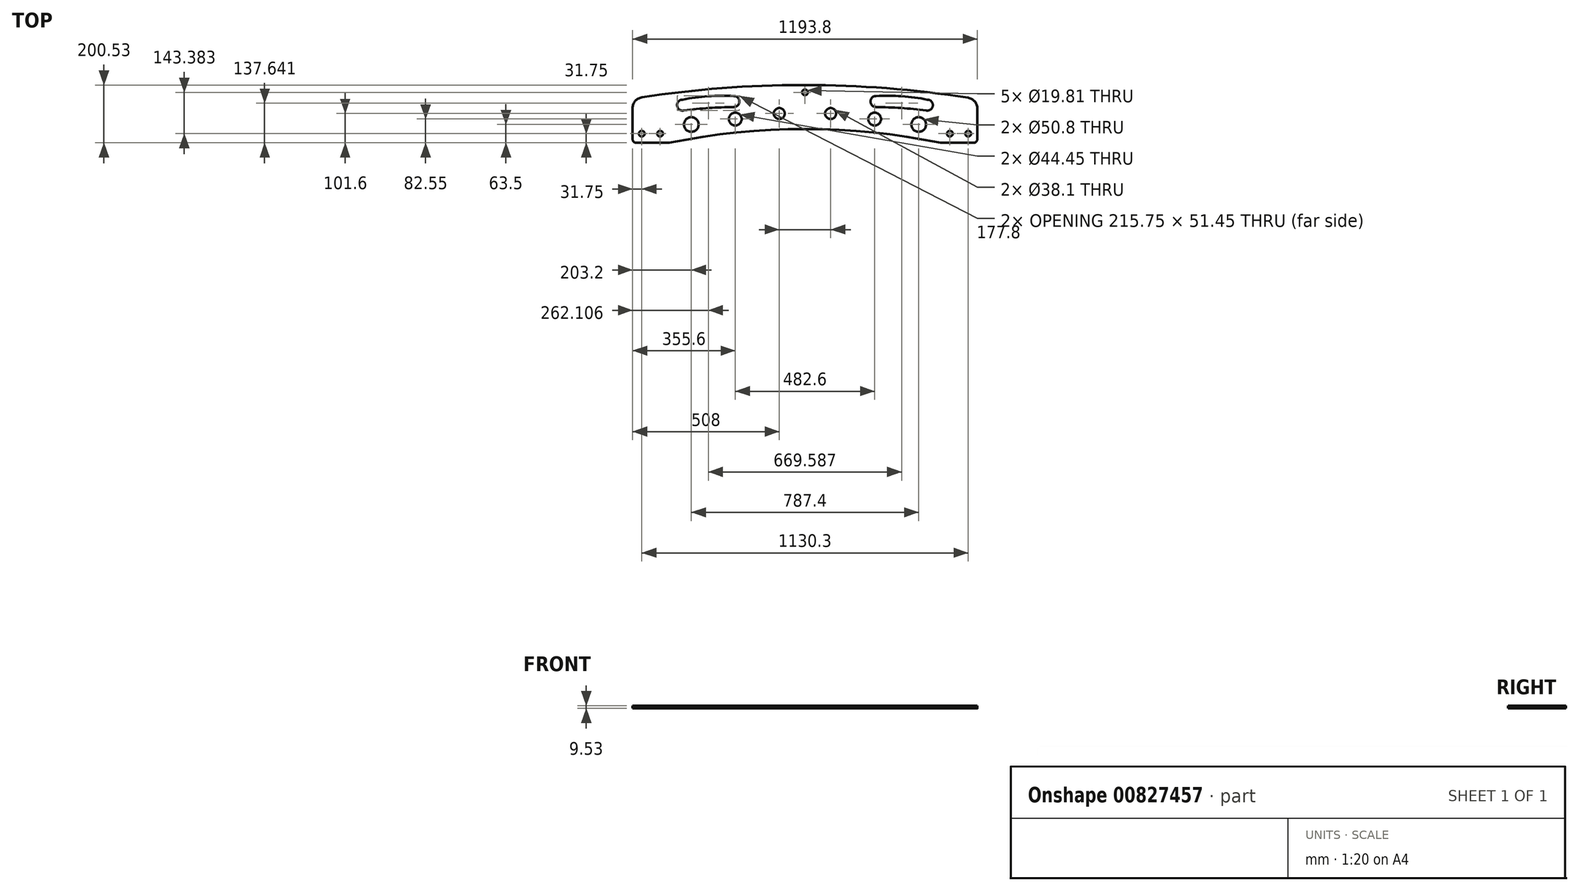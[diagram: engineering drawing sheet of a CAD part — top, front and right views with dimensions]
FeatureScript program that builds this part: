
annotation { "Feature Type Name" : "Feature", "Feature Type Description" : "" }
export const myFeature = defineFeature(function(context is Context, id is Id, definition is map)
    precondition{}
    {
        {
            var Q0;
            Q0=qCreatedBy(makeId("Top.planeOp"),FACE);
            var sketch = newSketch(context, id + "F0", { "sketchPlane" : qUnion([Q0])});
            skLineSegment(sketch, "E0.bottom", {"start": v(12.7, 0) * mm, "end": v(1181.1, 0) * mm});
            skLineSegment(sketch, "E0.top", {"start": v(-12.7, 200.53) * mm, "end": v(1206.5, 200.53) * mm});
            skLineSegment(sketch, "E0.left", {"start": v(0, 12.7) * mm, "end": v(0, 120.02) * mm});
            skLineSegment(sketch, "E0.right", {"start": v(1193.8, 12.7) * mm, "end": v(1193.8, 118.67) * mm});
            skPoint(sketch, "E1", {"position": v(127, 0) * mm});
            skPoint(sketch, "E2", {"position": v(1066.8, 0) * mm});
            skPoint(sketch, "E3", {"position": v(596.9, 0) * mm});
            skPoint(sketch, "E4", {"position": v(596.9, 48.13) * mm});
            skArc(sketch, "E5", {"start": v(1066.8, 0) * mm, "mid": v(596.9, 48.13) * mm, "end": v(127, 0) * mm});
            skPoint(sketch, "E6", {"position": v(0, 152.4) * mm});
            skPoint(sketch, "E7", {"position": v(1193.8, 152.4) * mm});
            skPoint(sketch, "E8", {"position": v(596.9, 200.53) * mm});
            skArc(sketch, "E9", {"start": v(1161.59, 156.31) * mm, "mid": v(597, 200.53) * mm, "end": v(32.3, 157.67) * mm});
            skPoint(sketch, "E10.visualSharp", {"position": v(0, 0) * mm});
            skArc(sketch, "E10.filletArc", {"start": v(0, 12.7) * mm, "mid": v(3.72, 3.72) * mm, "end": v(12.7, 0) * mm});
            skPoint(sketch, "E11.visualSharp", {"position": v(1193.8, 0) * mm});
            skArc(sketch, "E11.filletArc", {"start": v(1181.1, 0) * mm, "mid": v(1190.08, 3.72) * mm, "end": v(1193.8, 12.7) * mm});
            skCircle(sketch, "E12", {"center": v(596.9, 175.13) * mm, "radius": 9.9 * mm});
            skCircle(sketch, "E13", {"center": v(31.75, 31.75) * mm, "radius": 9.9 * mm});
            skCircle(sketch, "E14", {"center": v(1162.05, 31.75) * mm, "radius": 9.9 * mm});
            skArc(sketch, "E15", {"start": v(173.13, 149.73) * mm, "mid": v(154.23, 128.3) * mm, "end": v(177.88, 112.23) * mm});
            skArc(sketch, "E16", {"start": v(350.93, 124.33) * mm, "mid": v(369.98, 143.38) * mm, "end": v(350.93, 162.43) * mm});
            skArc(sketch, "E17", {"start": v(350.93, 124.33) * mm, "mid": v(261.85, 120.48) * mm, "end": v(173.13, 111.63) * mm});
            skArc(sketch, "E18", {"start": v(350.93, 162.43) * mm, "mid": v(261.64, 161.55) * mm, "end": v(173.13, 149.73) * mm});
            skLineSegment(sketch, "E19", {"start": v(596.9, 48.13) * mm, "end": v(596.9, 96.26) * mm, "construction": true});
            skArc(sketch, "E20.MirrorCS", {"start": v(842.87, 124.33) * mm, "mid": v(823.82, 143.38) * mm, "end": v(842.87, 162.43) * mm});
            skArc(sketch, "E21.MirrorCS", {"start": v(842.87, 162.43) * mm, "mid": v(932.16, 161.55) * mm, "end": v(1020.67, 149.73) * mm});
            skArc(sketch, "E22.MirrorCS", {"start": v(842.87, 124.33) * mm, "mid": v(931.95, 120.48) * mm, "end": v(1020.67, 111.63) * mm});
            skArc(sketch, "E23.MirrorCS", {"start": v(1020.67, 149.73) * mm, "mid": v(1039.57, 128.3) * mm, "end": v(1015.92, 112.23) * mm});
            skCircle(sketch, "E24", {"center": v(95.25, 31.75) * mm, "radius": 9.9 * mm});
            skCircle(sketch, "E25", {"center": v(1098.55, 31.75) * mm, "radius": 9.9 * mm});
            skPoint(sketch, "E26.newPointB", {"position": v(0, 203.2) * mm});
            skArc(sketch, "E26.filletArc", {"start": v(32.3, 157.67) * mm, "mid": v(9.18, 144.82) * mm, "end": v(0, 120.02) * mm});
            skArc(sketch, "E27.filletArc", {"start": v(1193.8, 118.67) * mm, "mid": v(1184.65, 143.44) * mm, "end": v(1161.59, 156.31) * mm});
            skCircle(sketch, "E28", {"center": v(203.2, 63.5) * mm, "radius": 25.4 * mm});
            skCircle(sketch, "E29", {"center": v(355.6, 82.55) * mm, "radius": 22.23 * mm});
            skCircle(sketch, "E30", {"center": v(508, 101.6) * mm, "radius": 19.05 * mm});
            skCircle(sketch, "E31.MirrorC", {"center": v(685.8, 101.6) * mm, "radius": 19.05 * mm});
            skCircle(sketch, "E32.MirrorC", {"center": v(838.2, 82.55) * mm, "radius": 22.23 * mm});
            skCircle(sketch, "E33.MirrorC", {"center": v(990.6, 63.5) * mm, "radius": 25.4 * mm});
            skSolve(sketch);
        }
        {
            var Q0;
            Q0=makeQuery(id+"F0.imprint","IMPRINT",FACE,{"disambiguationData":[TD([[makeQuery(id+"F0.imprint","IMPRINT",EDGE,{"derivedFrom":sQuery(id+"F0.wireOp",EDGE,"E0.left")}),-1.0]])]});
            extrude(context, id + "F1", {"entities" : qUnion([Q0]), "depth" : 9.52 * mm, "offsetDistance" : 25.4 * mm});
        }
    });
